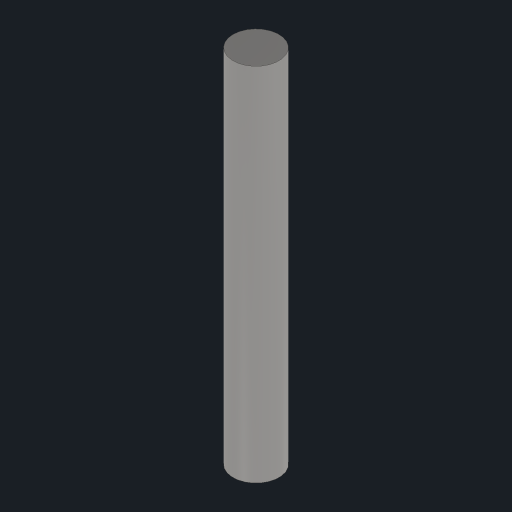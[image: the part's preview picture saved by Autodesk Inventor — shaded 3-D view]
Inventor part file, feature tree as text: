
AUTODESK INVENTOR PART (.ipt)
format: ipt  version: 2023.1 (Build 271208000, 208)  size: 78,336 bytes
history: native  units: mm
features: extrude x1, sketch x1
ambient origin geometry x8: Origin, YZ Plane, XZ Plane, XY Plane, X Axis, Y Axis, Z Axis, Center Point
bodies: Solid1 (feature_tree)
feature tree (2):
  extrude  "Extrusion1"  Depth=50.0mm TaperAngle=0.0deg
  sketch  "Sketch1"  dims[d0=6.35mm d1=50.0mm d2=0.0mm]
